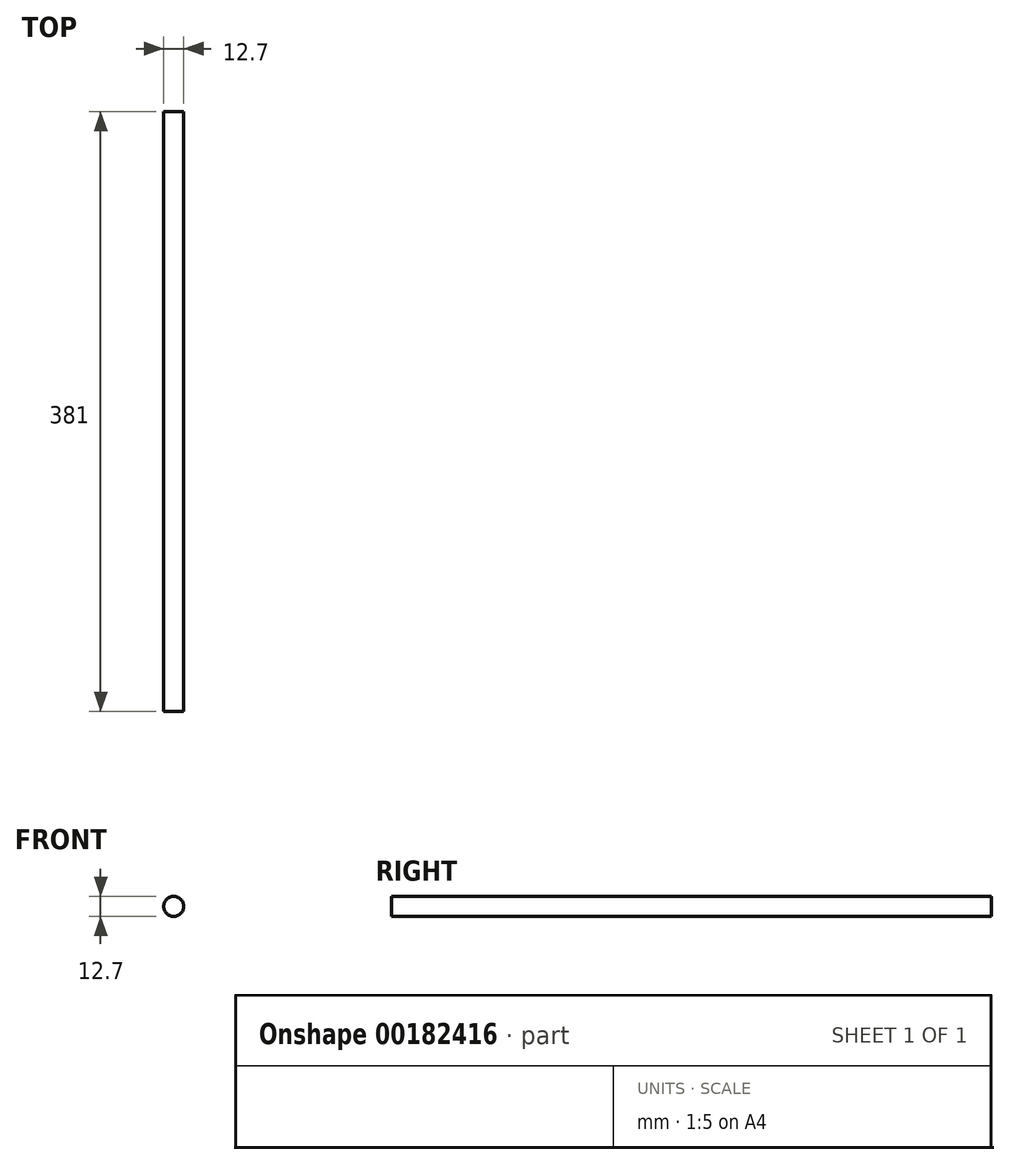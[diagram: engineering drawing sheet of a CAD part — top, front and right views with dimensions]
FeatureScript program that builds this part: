
annotation { "Feature Type Name" : "Feature", "Feature Type Description" : "" }
export const myFeature = defineFeature(function(context is Context, id is Id, definition is map)
    precondition{}
    {
        {
            var Q0;
            Q0=qCreatedBy(makeId("Front.planeOp"),FACE);
            var sketch = newSketch(context, id + "F0", { "sketchPlane" : qUnion([Q0])});
            skCircle(sketch, "E0", {"center": v(0, 0) * mm, "radius": 6.35 * mm});
            skSolve(sketch);
        }
        {
            var Q0;
            Q0=makeQuery(id+"F0.imprint","IMPRINT",FACE,{"disambiguationData":[TD([[makeQuery(id+"F0.imprint","IMPRINT",EDGE,{"derivedFrom":sQuery(id+"F0.wireOp",EDGE,"E0")}),1.0]])]});
            extrude(context, id + "F1", {"entities" : qUnion([Q0]), "depth" : 381 * mm});
        }
    });
